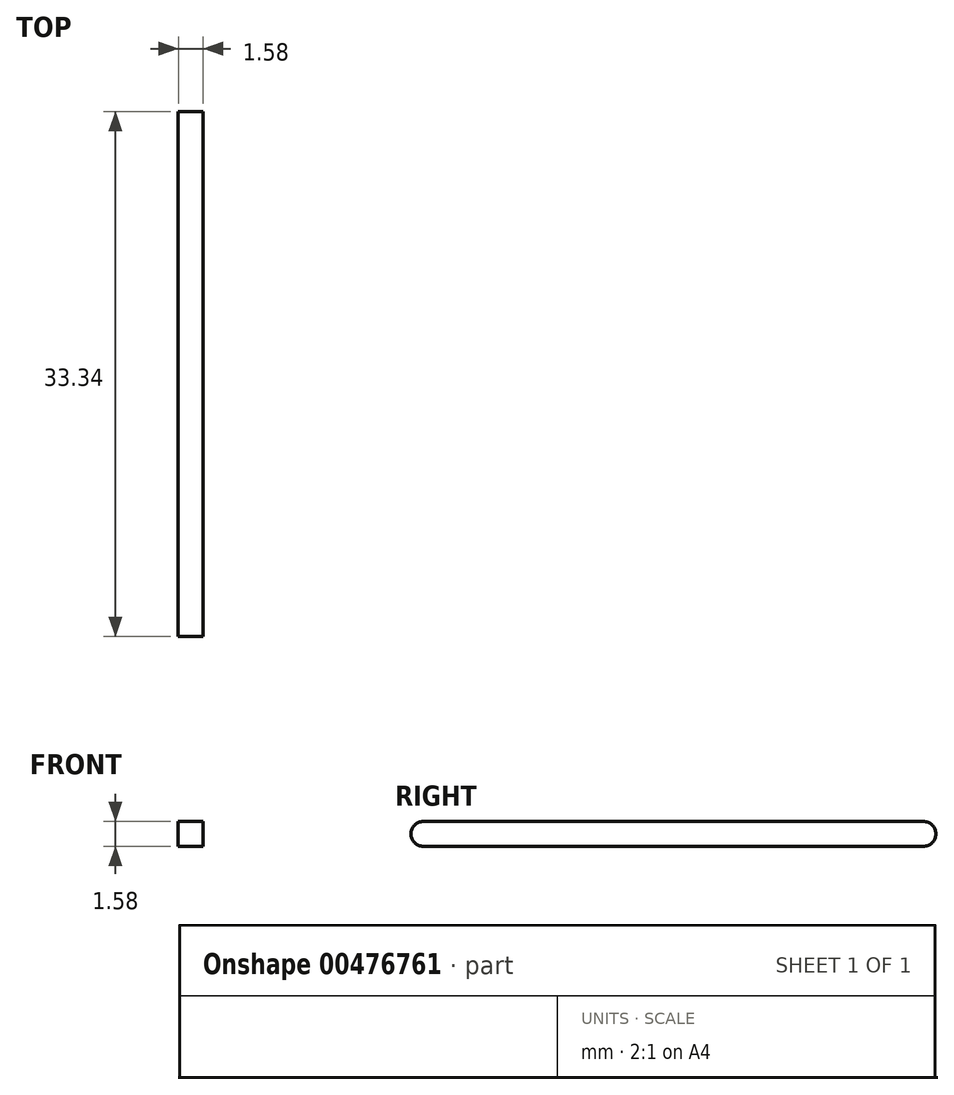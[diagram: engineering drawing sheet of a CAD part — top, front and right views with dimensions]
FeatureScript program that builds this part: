
annotation { "Feature Type Name" : "Feature", "Feature Type Description" : "" }
export const myFeature = defineFeature(function(context is Context, id is Id, definition is map)
    precondition{}
    {
        {
            var Q0;
            Q0=qCreatedBy(makeId("Right.planeOp"),FACE);
            var sketch = newSketch(context, id + "F0", { "sketchPlane" : qUnion([Q0])});
            skLineSegment(sketch, "E0.bottom", {"start": v(15.88, -0.8) * mm, "end": v(-15.88, -0.8) * mm});
            skLineSegment(sketch, "E0.top", {"start": v(15.88, 0.8) * mm, "end": v(-15.88, 0.8) * mm});
            skLineSegment(sketch, "E0.left", {"start": v(15.88, -0.8) * mm, "end": v(15.88, 0.8) * mm});
            skLineSegment(sketch, "E0.right", {"start": v(-15.88, -0.8) * mm, "end": v(-15.88, 0.8) * mm});
            skPoint(sketch, "E0.middle", {"position": v(0, 0) * mm});
            skCircle(sketch, "E1", {"center": v(-15.88, 0) * mm, "radius": 0.8 * mm});
            skCircle(sketch, "E2", {"center": v(15.88, 0) * mm, "radius": 0.8 * mm});
            skSolve(sketch);
        }
        {
            var Q0;
            {var subQ0=sQuery(id+"F0.wireOp",EDGE,"E0.right");Q0=makeQuery(id+"F0.imprint","IMPRINT",FACE,{"disambiguationData":[TD([[makeQuery(id+"F0.imprint","IMPRINT",EDGE,{"derivedFrom":subQ0}),1.0]])]});}
            var Q1;
            {var subQ0=sQuery(id+"F0.wireOp",EDGE,"E0.right");Q1=makeQuery(id+"F0.imprint","IMPRINT",FACE,{"disambiguationData":[TD([[makeQuery(id+"F0.imprint","IMPRINT",EDGE,{"derivedFrom":subQ0}),-1.0]])]});}
            var Q2;
            {var subQ0=sQuery(id+"F0.wireOp",EDGE,"E0.bottom");Q2=makeQuery(id+"F0.imprint","IMPRINT",FACE,{"disambiguationData":[TD([[makeQuery(id+"F0.imprint","IMPRINT",EDGE,{"derivedFrom":subQ0}),-1.0]])]});}
            var Q3;
            {var subQ0=sQuery(id+"F0.wireOp",EDGE,"E0.left");Q3=makeQuery(id+"F0.imprint","IMPRINT",FACE,{"disambiguationData":[TD([[makeQuery(id+"F0.imprint","IMPRINT",EDGE,{"derivedFrom":subQ0}),1.0]])]});}
            var Q4;
            {var subQ0=sQuery(id+"F0.wireOp",EDGE,"E0.left");Q4=makeQuery(id+"F0.imprint","IMPRINT",FACE,{"disambiguationData":[TD([[makeQuery(id+"F0.imprint","IMPRINT",EDGE,{"derivedFrom":subQ0}),-1.0]])]});}
            extrude(context, id + "F1", {"entities" : qUnion([Q0, Q1, Q2, Q3, Q4]), "depth" : 1.59 * mm, "symmetric" : true});
        }
    });
